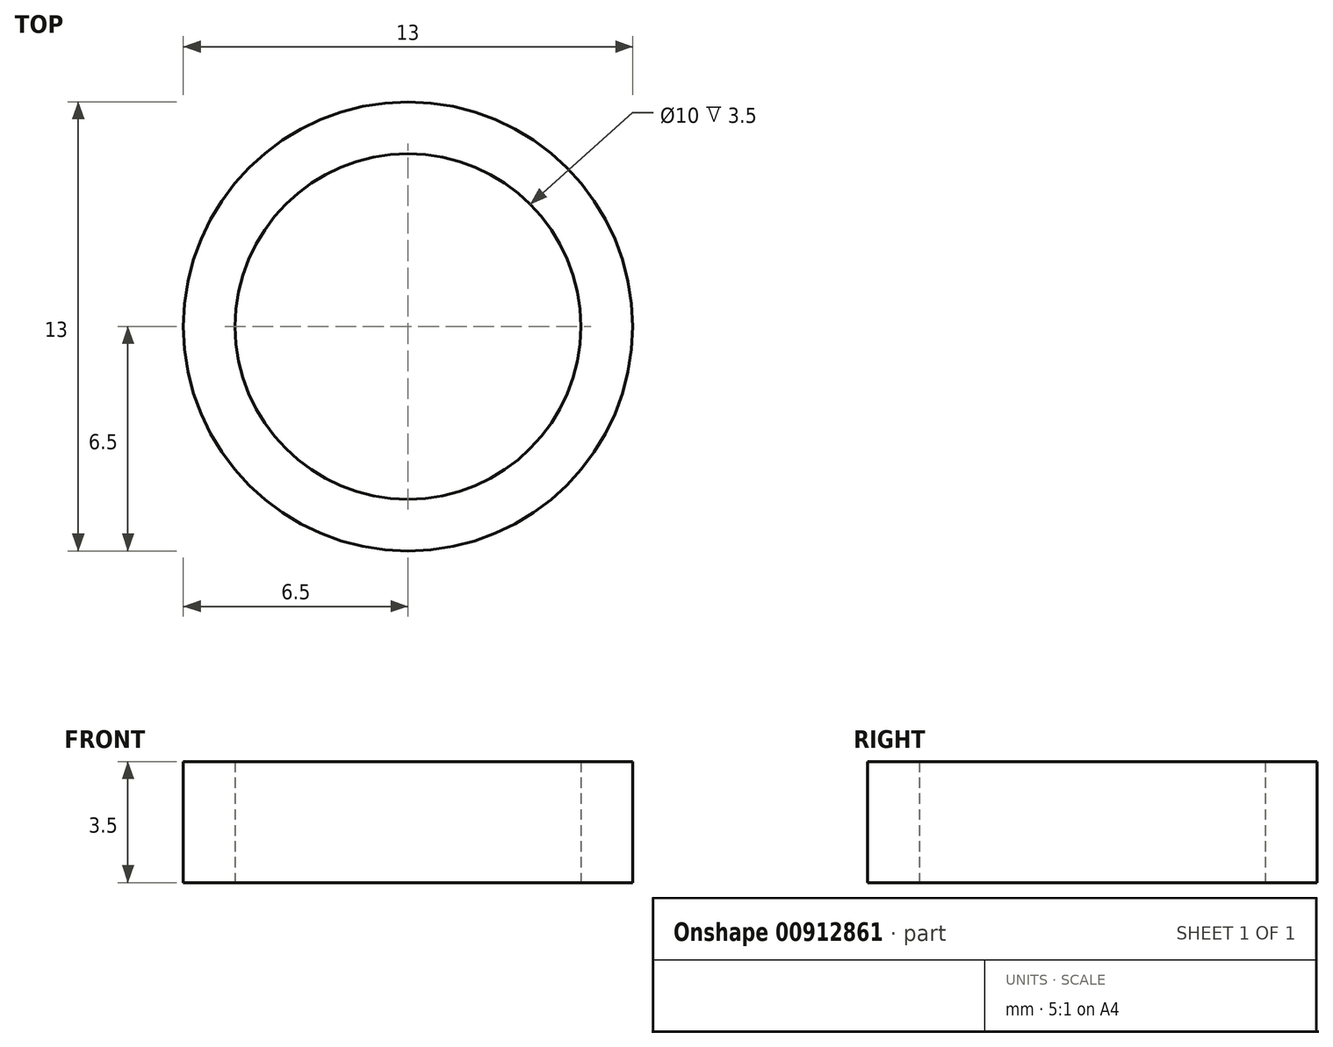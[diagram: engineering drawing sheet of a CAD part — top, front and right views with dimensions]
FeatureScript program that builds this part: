
annotation { "Feature Type Name" : "Feature", "Feature Type Description" : "" }
export const myFeature = defineFeature(function(context is Context, id is Id, definition is map)
    precondition{}
    {
        {
            var Q0;
            Q0=qCreatedBy(makeId("Top.planeOp"),FACE);
            var sketch = newSketch(context, id + "F0", { "sketchPlane" : qUnion([Q0])});
            skCircle(sketch, "E0", {"center": v(0, 0) * mm, "radius": 6.5 * mm});
            skCircle(sketch, "E1", {"center": v(0, 0) * mm, "radius": 5 * mm});
            skSolve(sketch);
        }
        {
            var Q0;
            Q0=makeQuery(id+"F0.imprint","IMPRINT",FACE,{"disambiguationData":[TD([[makeQuery(id+"F0.imprint","IMPRINT",EDGE,{"derivedFrom":sQuery(id+"F0.wireOp",EDGE,"E0")}),1.0]])]});
            extrude(context, id + "F1", {"entities" : qUnion([Q0]), "depth" : 3.5 * mm, "offsetDistance" : 25 * mm});
        }
    });
